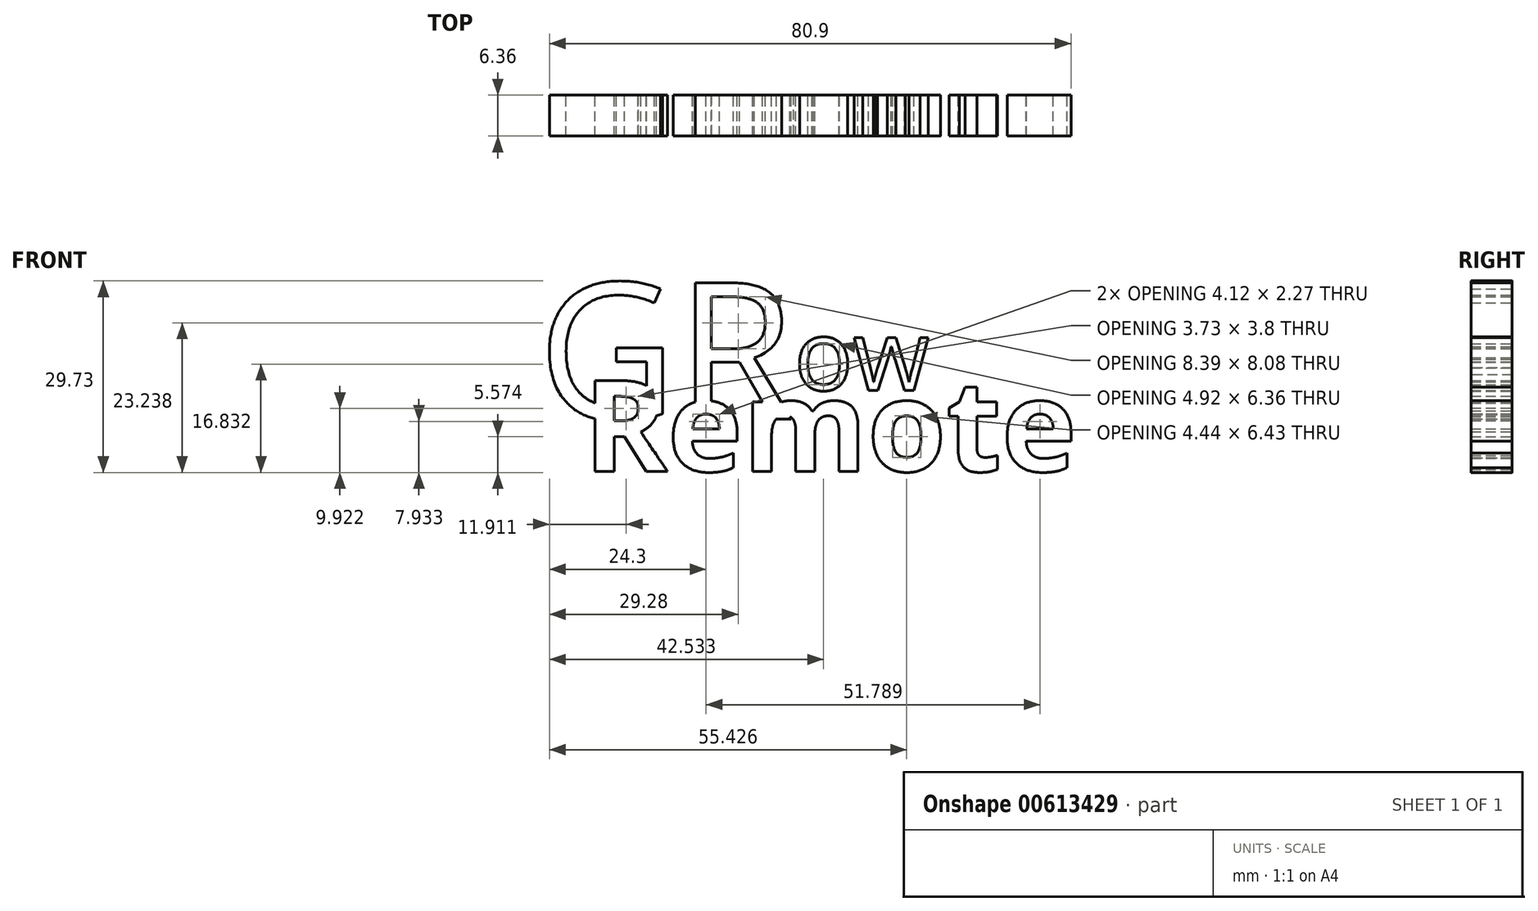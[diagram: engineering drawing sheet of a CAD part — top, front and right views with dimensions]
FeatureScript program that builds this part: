
annotation { "Feature Type Name" : "Feature", "Feature Type Description" : "" }
export const myFeature = defineFeature(function(context is Context, id is Id, definition is map)
    precondition{}
    {
        {
            var Q0;
            Q0=qCreatedBy(makeId("Front.planeOp"),FACE);
            var sketch = newSketch(context, id + "F0", { "sketchPlane" : qUnion([Q0])});
            skText(sketch, "E0", { "text": "GR", "fontName": "OpenSans-Regular.ttf"});
            skText(sketch, "E1", { "text": "Remote", "fontName": "OpenSans-Bold.ttf"});
            skText(sketch, "E2", { "text": "ow", "fontName": "OpenSans-Regular.ttf"});
            const initialGuessF0  = {"E0": [-0.03737, -0.0112, 1, 0, 0.0213], "E1": [-0.03027, -0.01932, 1, 0, 0.0142], "E2": [0.00238, -0.00674, 1, 0, 0.01095]};
            skSetInitialGuess(sketch, initialGuessF0);
            skSolve(sketch);
        }
        {
            var Q0;
            Q0 = qSketchRegion(id + "F0", true);
            extrude(context, id + "F1", {"entities" : qUnion([Q0]), "endBound" : BoundingType.SYMMETRIC, "depth" : 6.35 * mm, "offsetDistance" : 25.4 * mm});
        }
    });
